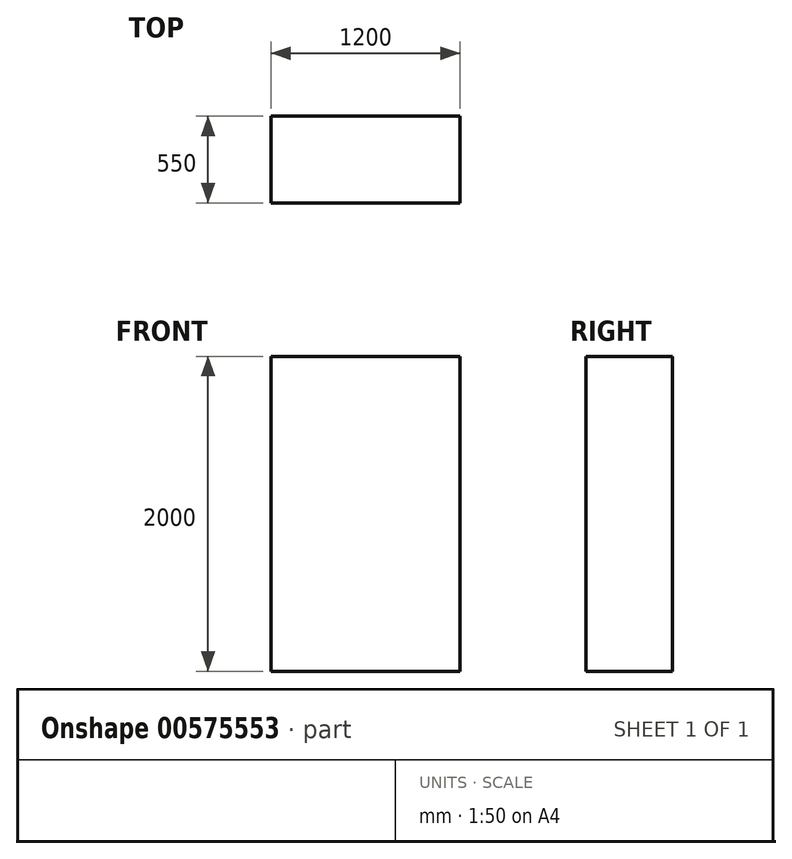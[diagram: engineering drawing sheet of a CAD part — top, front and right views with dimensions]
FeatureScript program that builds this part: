
annotation { "Feature Type Name" : "Feature", "Feature Type Description" : "" }
export const myFeature = defineFeature(function(context is Context, id is Id, definition is map)
    precondition{}
    {
        {
            var Q0;
            Q0=qCreatedBy(makeId("Top.planeOp"),FACE);
            var sketch = newSketch(context, id + "F0", { "sketchPlane" : qUnion([Q0])});
            skLineSegment(sketch, "E0.bottom", {"start": v(0, 0) * mm, "end": v(-1200, 0) * mm});
            skLineSegment(sketch, "E0.top", {"start": v(0, 550) * mm, "end": v(-1200, 550) * mm});
            skLineSegment(sketch, "E0.left", {"start": v(0, 0) * mm, "end": v(0, 550) * mm});
            skLineSegment(sketch, "E0.right", {"start": v(-1200, 0) * mm, "end": v(-1200, 550) * mm});
            skSolve(sketch);
        }
        {
            var Q0;
            Q0 = qSketchRegion(id + "F0", true);
            extrude(context, id + "F1", {"entities" : qUnion([Q0]), "depth" : 2000 * mm, "offsetDistance" : 25 * mm});
        }
    });
